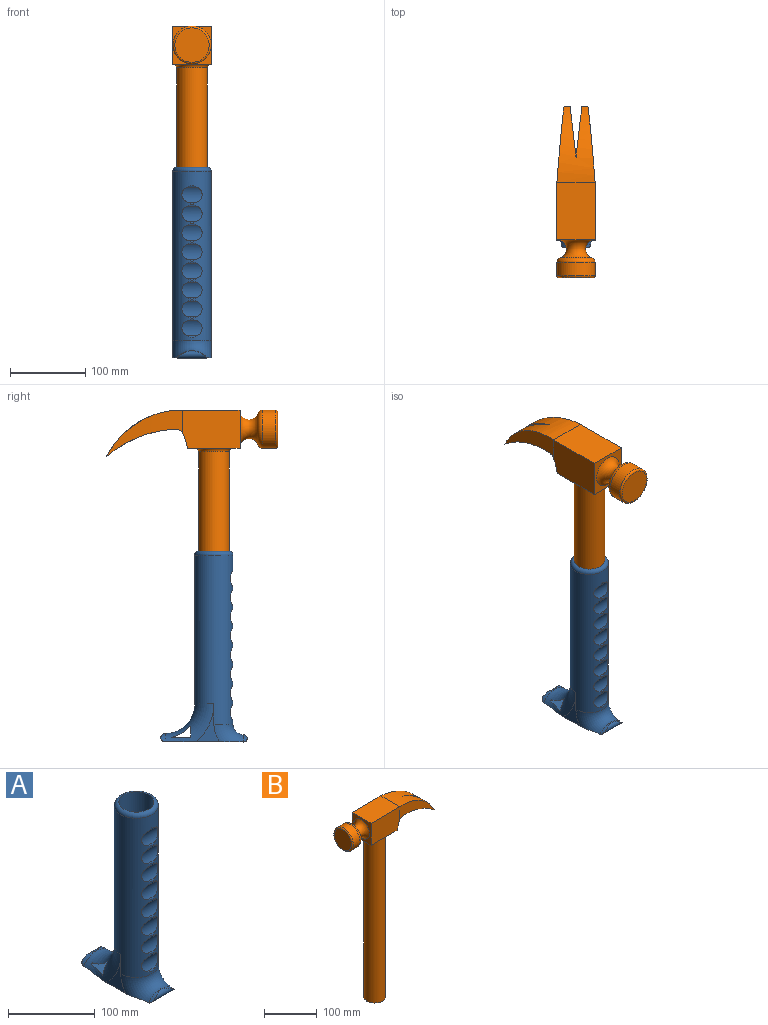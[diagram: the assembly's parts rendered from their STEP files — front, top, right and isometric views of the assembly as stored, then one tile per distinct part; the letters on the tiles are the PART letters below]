
ASSEMBLY  parts=2 mates=1
PART A: 46 faces, bbox 55.5x115.6x293.7 mm
  f0: plane 104.78x50.82mm, normal (0,0,-1), area 4973.9mm2, adj f1,f3,f4,f5,f37,f40,f41,f42
  f1: cylinder r=4.76mm len=39.66mm, axis (-1,0,0), area 391.5mm2, adj f0,f41,f42
  f2: cylinder r=4.76mm len=0.03mm, axis (-1,0,0), area 0mm2, adj f40,f41,f42
  f3: plane 50.8x32.35mm, normal (-1,0,0), area 436.6mm2, adj f0,f36,f37,f40
  f4: plane 50.8x32.35mm, normal (1,0,0), area 436.6mm2, adj f0,f36,f37,f40
  f5: cylinder r=5.56mm len=42mm, axis (-1,0,0), area 487.7mm2, adj f0,f38,f39
  f6: cylinder r=5.08mm len=12.92mm, axis (-1,0,0), area 19.1mm2, adj f7,f36
  f7: cylinder r=18.11mm len=26.76mm, axis (-1,0,0), area 480.6mm2, adj f6,f8,f36
  f8: cylinder r=5.08mm len=12.92mm, axis (-1,0,0), area 19.1mm2, adj f7,f9,f36
  f9: cylinder r=5.08mm len=12.92mm, axis (-1,0,0), area 19.1mm2, adj f8,f10,f36
  f10: cylinder r=18.11mm len=26.76mm, axis (-1,0,0), area 480.6mm2, adj f9,f11,f36
  f11: cylinder r=5.08mm len=12.92mm, axis (-1,0,0), area 19.1mm2, adj f10,f12,f36
  f12: cylinder r=5.08mm len=12.92mm, axis (-1,0,0), area 19.1mm2, adj f11,f13,f36
  f13: cylinder r=18.11mm len=26.76mm, axis (-1,0,0), area 480.6mm2, adj f12,f14,f36
  f14: cylinder r=5.08mm len=12.92mm, axis (-1,0,0), area 19.1mm2, adj f13,f15,f36
  f15: cylinder r=5.08mm len=12.92mm, axis (-1,0,0), area 19.1mm2, adj f14,f16,f36
  f16: cylinder r=18.11mm len=26.76mm, axis (-1,0,0), area 480.6mm2, adj f15,f17,f36
  f17: cylinder r=5.08mm len=12.92mm, axis (-1,0,0), area 19.1mm2, adj f16,f18,f36
  f18: cylinder r=5.08mm len=12.92mm, axis (-1,0,0), area 19.1mm2, adj f17,f19,f36
  f19: cylinder r=18.11mm len=26.76mm, axis (-1,0,0), area 480.6mm2, adj f18,f20,f36
  f20: cylinder r=5.08mm len=12.92mm, axis (-1,0,0), area 19.1mm2, adj f19,f21,f36
  f21: cylinder r=5.08mm len=12.92mm, axis (-1,0,0), area 19.1mm2, adj f20,f22,f36
  f22: cylinder r=18.11mm len=26.76mm, axis (-1,0,0), area 480.6mm2, adj f21,f23,f36
  f23: cylinder r=5.08mm len=12.92mm, axis (-1,0,0), area 19.1mm2, adj f22,f24,f36
  f24: cylinder r=5.08mm len=12.92mm, axis (-1,0,0), area 19.1mm2, adj f23,f25,f36
  f25: cylinder r=18.11mm len=26.76mm, axis (-1,0,0), area 480.6mm2, adj f24,f26,f36
  f26: cylinder r=5.08mm len=12.92mm, axis (-1,0,0), area 19.1mm2, adj f25,f27,f36
  f27: cylinder r=5.08mm len=12.92mm, axis (-1,0,0), area 19.1mm2, adj f26,f28,f36
  f28: cylinder r=18.11mm len=26.76mm, axis (-1,0,0), area 480.6mm2, adj f27,f29,f36
  f29: cylinder r=5.08mm len=12.92mm, axis (-1,0,0), area 19.1mm2, adj f28,f36
  f30: cylinder r=0.51mm len=47.71mm, axis (-1,0,0), area 38mm2, adj f31,f35,f37
  f31: plane 48.16x14.23mm, normal (0,1,0), area 572.3mm2, adj f30,f32,f37
  f32: cylinder r=0.51mm len=33.8mm, axis (-1,0,0), area 39.9mm2, adj f31,f33,f37
  f33: cylinder r=45.24mm len=31.71mm, axis (-1,0,0), area 881.5mm2, adj f32,f34,f37
  f34: cylinder r=0.51mm len=34.07mm, axis (-1,0,0), area 49mm2, adj f33,f35,f37
  f35: plane 47.72x24.04mm, normal (0,0,1), area 985.3mm2, adj f30,f34,f37
  f36: cylinder r=25.4mm len=225.09mm, axis (0,0,1), area 29663.5mm2, adj f3,f4,f6,f7,f8,f9,f10,f11
  f37: torus R=65.09mm, axis (1,0,0), area 4876.4mm2, adj f0,f3,f4,f30,f31,f32,f33,f34
  f38: cylinder r=25.4mm len=21mm, axis (0,-1,0), area 92.3mm2, adj f5,f37
  f39: cylinder r=25.4mm len=21mm, axis (0,-1,0), area 92.3mm2, adj f5,f37
  f40: torus R=39.71mm, axis (-1,0,0), area 2210.4mm2, adj f0,f2,f3,f4,f36,f41,f42
  f41: cylinder r=25.4mm len=19.83mm, axis (0,1,0), area 72.9mm2, adj f0,f1,f2,f40
  f42: cylinder r=25.4mm len=19.83mm, axis (0,1,0), area 72.9mm2, adj f0,f1,f2,f40
  f43: cylinder r=20.32mm len=243.84mm, axis (0,0,1), area 31132.1mm2, adj f44,f45
  f44: plane 40.64x40.64mm, normal (0,0,1), area 1297.2mm2, adj f43
  f45: torus R=20.32mm, axis (0,0,-1), area 1180.9mm2, adj f36,f43
PART B: 22 faces, bbox 228x62.8x433.9 mm
  f0: plane 50.8x34.77mm, normal (0,0,-1), area 752.7mm2, adj f1,f2,f5,f21
  f1: plane 76.93x50.8mm, normal (0,-1,0), area 3818.7mm2, adj f0,f3,f4,f5,f6,f9,f15
  f2: plane 76.93x50.8mm, normal (0,1,0), area 3818.7mm2, adj f0,f3,f4,f5,f6,f9,f18
  f3: plane 50.8x50.8mm, normal (-1,0,0), area 1173.1mm2, adj f1,f2,f4,f9,f10
  f4: plane 50.8x34.77mm, normal (0,0,-1), area 752.7mm2, adj f1,f2,f3,f21
  f5: plane 50.8x16.13mm, normal (0.96,0,-0.28), area 853.3mm2, adj f0,f1,f2,f6
  f6: cylinder r=12.7mm len=50.8mm, axis (0,1,0), area 852.5mm2, adj f1,f2,f5,f7,f15,f18
  f7: cylinder r=148.1mm len=90.88mm, axis (0,1,0), area 3448.4mm2, adj f6,f8,f15,f16,f17,f18
  f8: cylinder r=112.94mm len=100.98mm, axis (0,1,0), area 4317.7mm2, adj f7,f9,f15,f16,f17,f18
  f9: plane 76.93x50.8mm, normal (0,0,1), area 3907.9mm2, adj f1,f2,f3,f8
  f10: torus R=25.4mm, axis (1,0,0), area 3079mm2, adj f3,f11
  f11: torus R=19.05mm, axis (1,0,0), area 1174.5mm2, adj f10,f12
  f12: cylinder r=25.4mm len=50.8mm, axis (1,0,0), area 2808.8mm2, adj f11,f13
  f13: torus R=22.86mm, axis (1,0,0), area 613.6mm2, adj f12,f14
  f14: plane 45.72x45.72mm, normal (-1,0,0), area 1641.7mm2, adj f13
  f15: extruded ~100.98x62.36mm, area 1928.6mm2, adj f1,f6,f7,f8
  f16: plane 67.71x57.35mm, normal (0.12,0.99,0), area 1094.3mm2, adj f7,f8,f17
  f17: plane 67.71x57.35mm, normal (0.12,-0.99,0), area 1094.3mm2, adj f7,f8,f16
  f18: extruded ~100.98x62.36mm, area 1928.5mm2, adj f2,f6,f7,f8
  f19: cylinder r=20.32mm len=375.92mm, axis (0,0,1), area 47995.3mm2, adj f20,f21
  f20: plane 40.64x40.64mm, normal (0,0,-1), area 1297.2mm2, adj f19
  f21: torus R=25.4mm, axis (0,0,-1), area 1111.3mm2, adj f0,f4,f19
PLACE A at identity
PLACE B rot(axis=(0,0,1),90deg) t=(0,4.06,289.56)mm
MATE fastened B.f19 <-> A.f43  axis (0,0,-1) through (0,0,-116.84)mm
